# Revit family: IS_Hotline_K2760_BIM_DE
name_source: partatom
category: Plumbing Fixtures
revit_build: Autodesk Revit MEP 2016 (Build: 20161004_0715(x64)
units: mm (PartAtom-declared; Revit-internal decimal feet)

## family parameters
Always vertical = No
Cut with Voids When Loaded = No
OmniClass Number = 23.45.05.14.21
OmniClass Title = Bathtubs
Part Type = Normal
Room Calculation Point = No
Round Connector Dimension = Use Diameter
Shared = No
Work Plane-Based = No

## types (1)
- K276001 HOTLINE NEU panel for shower bath tub 1600x910mm
    Accessories = www.idealstandard.de\ersatzteile
    AssetType = Fixed
    BIMObjectName = ISI_IdealStandard_Baths_Hotline_K276010
    BIMobject category = Screens & Dividers
    BOSUseNativeGeometries = 1
    BarCode = 4015413057691
    Brand = Ideal Standard
    Brand url = http://www.idealstandard.de
    ConnectionType = Plumbing
    Cost = 0 $
    CurrencyUnit = €
    CurrentRevision = 1
    Date of publishing = 20/12/2017
    DrainSize = 0 mm  [stored 0 ft]
    DurationUnit = Year
    EAN code = https://4015413057691
    Edition number = 1
    IFC Classification = Sanitary Terminal
    IfcExportAs = IfcSanitaryTerminalType
    Installation instructions = http://www.idealstandard.de
    InstallationInstructions = www.idealstandard.de\produkte
    MaintenanceInformation = www.idealstandard.de\produkte
    Manufacturer name = Ideal Standard
    ManufacturerURL = http://www.idealstandard.de
    Material main = Acrylic
    MaterialThickness = 0 mm  [stored 0 ft]
    Model = K276010
    ModelNumber = K276010
    NBS Reference Code = 35-06-08
    NBS Reference Description = Baths
    Name = Baths_Hotline_K276010
    NettWeight = 5 Kg
    Nominal height = 565
    Nominal width = 1600
    NominalDepth = 1600 mm  [stored 5.24934 ft]
    NominalHeight = 565 mm  [stored 1.85367 ft]
    NominalLength = 1600 mm  [stored 5.24934 ft]
    NominalWidth = 910 mm
    OmniClass Code = 23-31 15 00
    OmniClass Description = Bathtubs
    Product Guid = cc8481f4-5bb3-49ec-824d-0ce279a245a9
    Product SKU = K2760
    Product data url = https://bimobject.com
    Product family = Sanitary
    Product group = Bath Panel
    Product name = HOTLINE NEU panel for shower bath tub 1600x910mm
    Product url = http://www.idealstandard.de
    ProductInformation = www.idealstandard.de/produkte
    QR code = http://bimobject.com
    Size = 1600x910x565 mm
    Space = Internal
    SpareParts = www.idealstandard.de/ersatzteile
    Technical description = http://www.idealstandard.de
    URL = http://www.idealstandard.de
    Uniclass 1.4 Code = L7211
    Uniclass 1.4 Description = Baths
    Uniclass 2.0 Code = PR-35-06-08
    Uniclass 2.0 Description = Baths
    Uniclass 2015 Code = Pr_40_20_06_08
    Uniclass 2015 Name = Baths
    Uniclass2015Code = Pr_40_20_06_08
    Uniclass2015Title = Baths
    Uniclass2015Version = Products v1.1
    Version = 1
    VolumeUnits = Litres
    Weight Net (Kg) = 5

note: [stored X ft] marks values corroborated as IEEE doubles in the binary element streams (Revit-internal decimal feet)

## geometry (parser evidence)
native form markers: Blend x4, Sweep x1
no freeform markers — native parametric forms only
